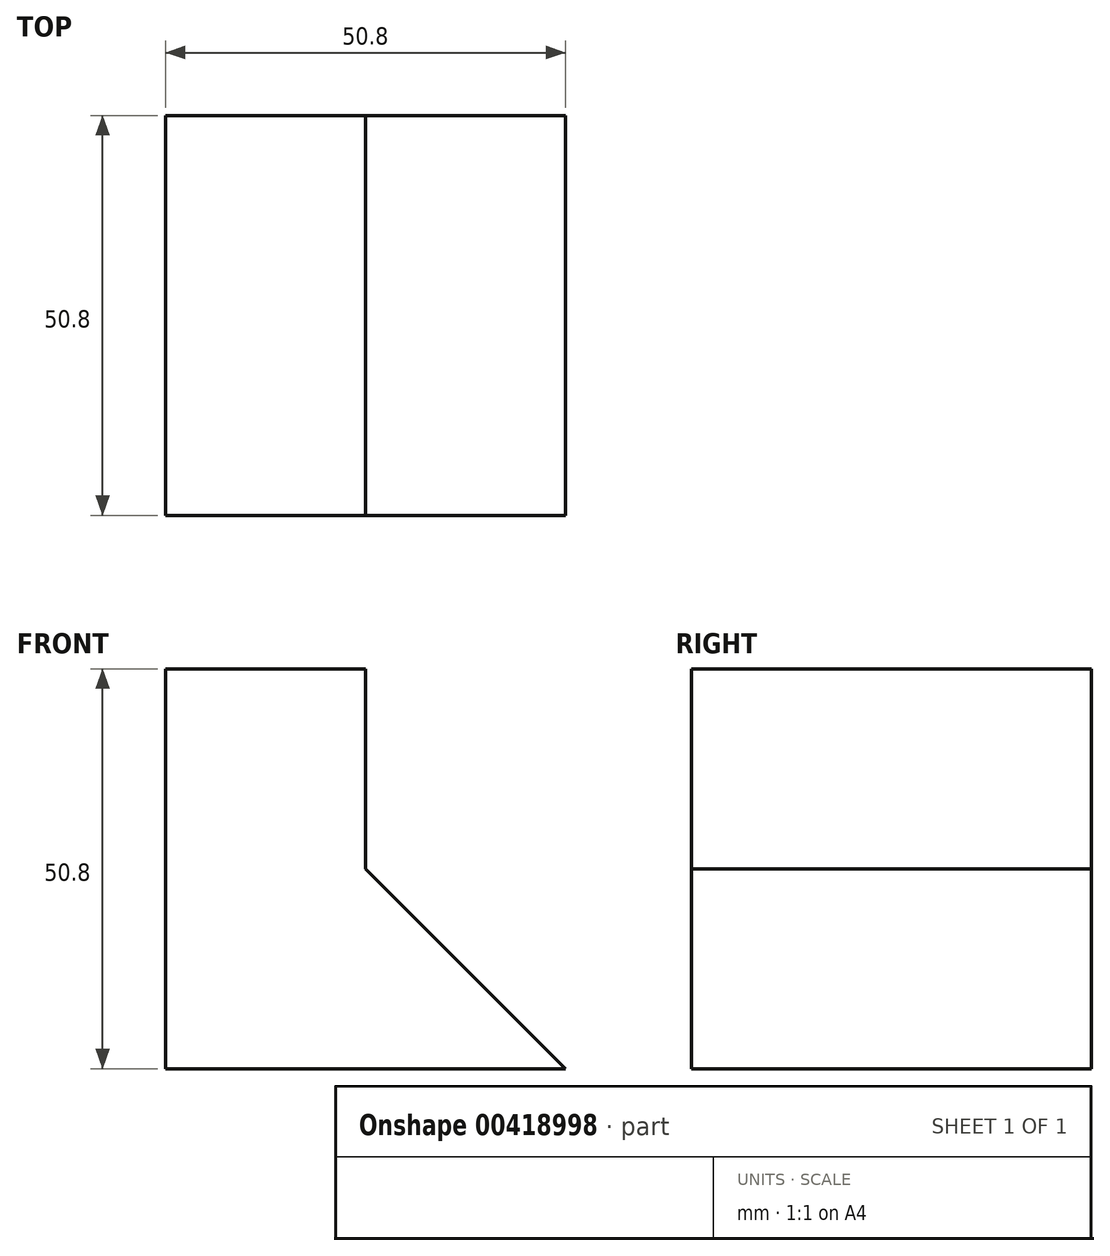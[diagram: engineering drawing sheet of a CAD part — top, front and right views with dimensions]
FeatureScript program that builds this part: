
annotation { "Feature Type Name" : "Feature", "Feature Type Description" : "" }
export const myFeature = defineFeature(function(context is Context, id is Id, definition is map)
    precondition{}
    {
        {
            var Q0;
            Q0=qCreatedBy(makeId("Front.planeOp"),FACE);
            var sketch = newSketch(context, id + "F0", { "sketchPlane" : qUnion([Q0])});
            skLineSegment(sketch, "E0", {"start": v(0, 0) * mm, "end": v(-50.8, 0) * mm});
            skLineSegment(sketch, "E1", {"start": v(-50.8, 0) * mm, "end": v(-50.8, 50.8) * mm});
            skLineSegment(sketch, "E2", {"start": v(-50.8, 50.8) * mm, "end": v(-25.4, 50.8) * mm});
            skLineSegment(sketch, "E3", {"start": v(-25.4, 50.8) * mm, "end": v(-25.4, 25.4) * mm});
            skLineSegment(sketch, "E4", {"start": v(-25.4, 25.4) * mm, "end": v(0, 0) * mm});
            skSolve(sketch);
        }
        {
            var Q0;
            Q0=makeQuery(id+"F0.imprint","IMPRINT",FACE,{"disambiguationData":[TD([[makeQuery(id+"F0.imprint","IMPRINT",EDGE,{"derivedFrom":sQuery(id+"F0.wireOp",EDGE,"E0")}),-1.0]])]});
            extrude(context, id + "F1", {"entities" : qUnion([Q0]), "depth" : 50.8 * mm});
        }
    });
